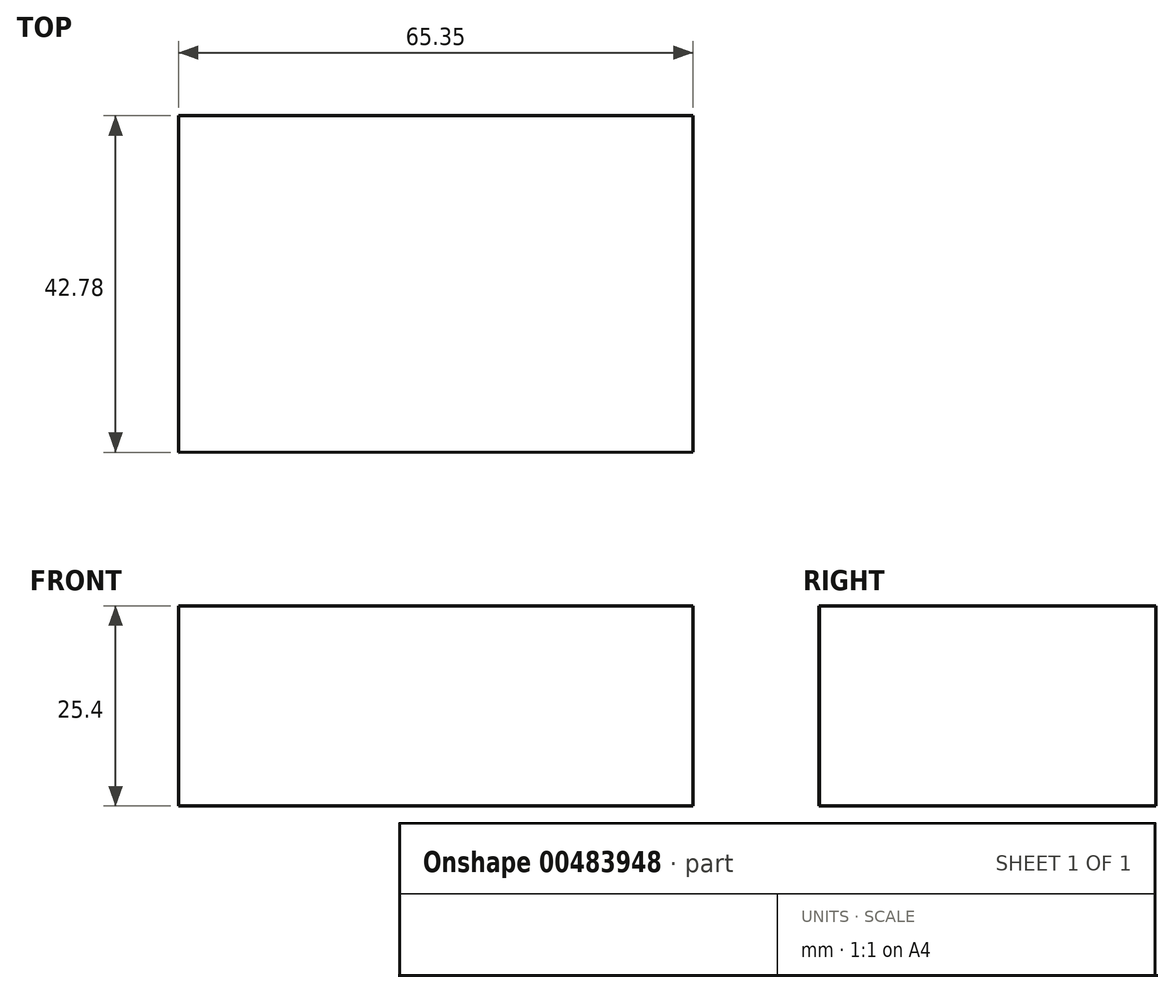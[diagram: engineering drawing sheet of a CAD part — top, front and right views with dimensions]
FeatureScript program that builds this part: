
annotation { "Feature Type Name" : "Feature", "Feature Type Description" : "" }
export const myFeature = defineFeature(function(context is Context, id is Id, definition is map)
    precondition{}
    {
        {
            var Q0;
            Q0=qCreatedBy(makeId("Top.planeOp"),FACE);
            var sketch = newSketch(context, id + "F0", { "sketchPlane" : qUnion([Q0])});
            skLineSegment(sketch, "E0", {"start": v(45.5, 6.9) * mm, "end": v(110.86, 6.9) * mm});
            skLineSegment(sketch, "E1", {"start": v(45.5, 6.9) * mm, "end": v(45.5, -35.87) * mm});
            skLineSegment(sketch, "E2", {"start": v(110.86, 6.9) * mm, "end": v(110.86, -35.79) * mm});
            skLineSegment(sketch, "E3", {"start": v(45.5, -35.87) * mm, "end": v(110.86, -35.79) * mm});
            skSolve(sketch);
        }
        {
            var Q0;
            Q0=makeQuery(id+"F0.imprint","IMPRINT",FACE,{"disambiguationData":[TD([[makeQuery(id+"F0.imprint","IMPRINT",EDGE,{"derivedFrom":sQuery(id+"F0.wireOp",EDGE,"E0")}),-1.0]])]});
            extrude(context, id + "F1", {"entities" : qUnion([Q0]), "depth" : 25.4 * mm});
        }
        {
            var Q0;
            Q0 = qSketchRegion(id + "F0", true);
            extrude(context, id + "F2", {"entities" : qUnion([Q0]), "operationType" : NewBodyOperationType.ADD, "depth" : 25.4 * mm});
        }
    });
